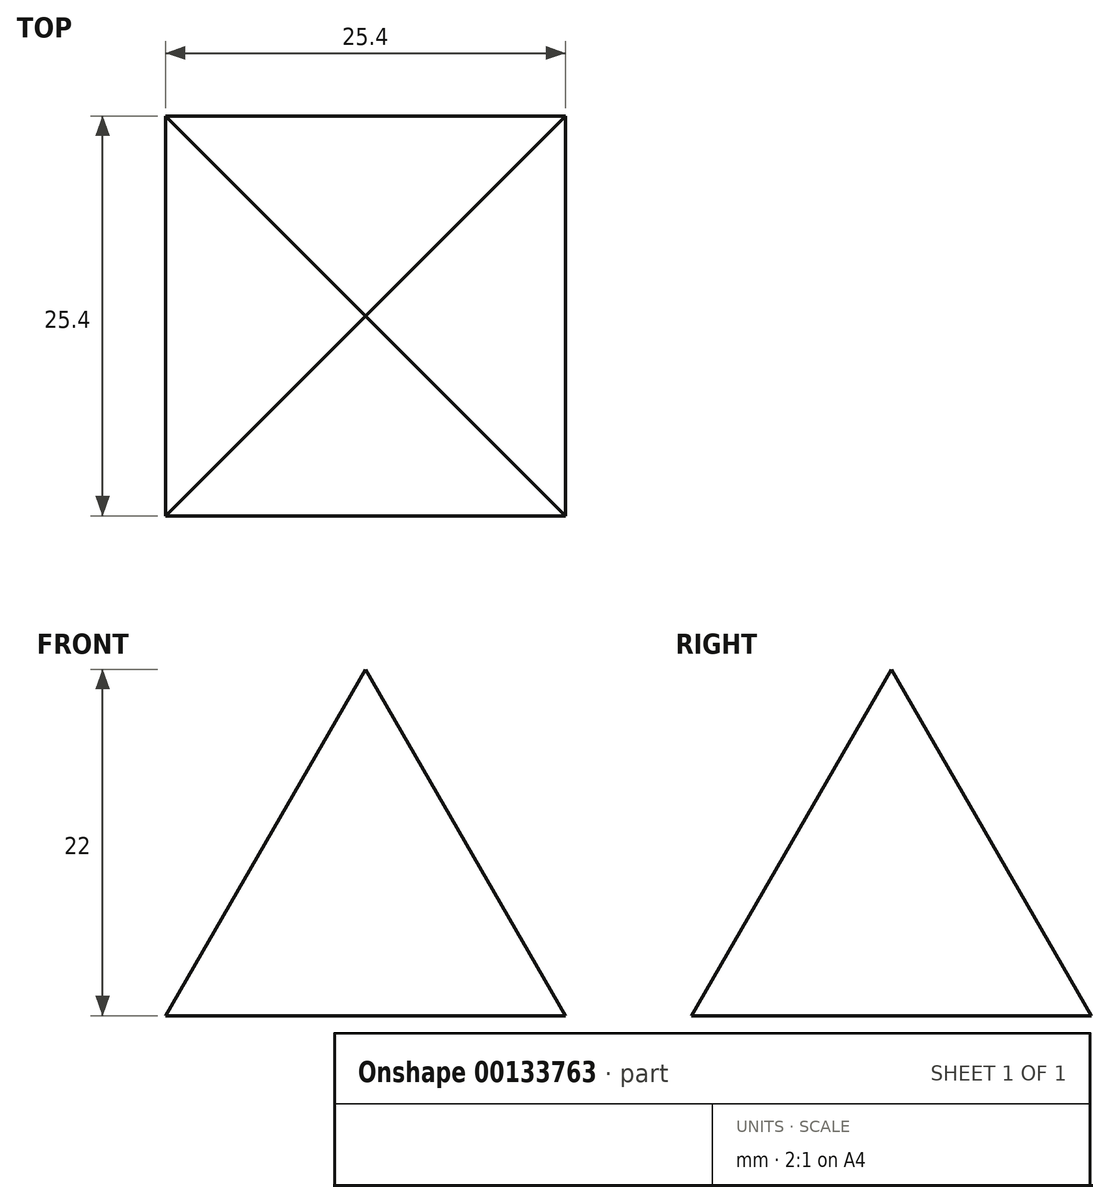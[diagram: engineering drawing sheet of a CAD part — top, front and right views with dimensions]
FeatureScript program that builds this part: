
annotation { "Feature Type Name" : "Feature", "Feature Type Description" : "" }
export const myFeature = defineFeature(function(context is Context, id is Id, definition is map)
    precondition{}
    {
        {
            var Q0;
            Q0=qCreatedBy(makeId("Top.planeOp"),FACE);
            var sketch = newSketch(context, id + "F0", { "sketchPlane" : qUnion([Q0])});
            skLineSegment(sketch, "E0.bottom", {"start": v(12.7, -12.7) * mm, "end": v(-12.7, -12.7) * mm});
            skLineSegment(sketch, "E0.top", {"start": v(12.7, 12.7) * mm, "end": v(-12.7, 12.7) * mm});
            skLineSegment(sketch, "E0.left", {"start": v(12.7, -12.7) * mm, "end": v(12.7, 12.7) * mm});
            skLineSegment(sketch, "E0.right", {"start": v(-12.7, -12.7) * mm, "end": v(-12.7, 12.7) * mm});
            skPoint(sketch, "E0.middle", {"position": v(0, 0) * mm});
            skSolve(sketch);
        }
        {
            var Q0;
            Q0=makeQuery(id+"F0.imprint","IMPRINT",FACE,{"disambiguationData":[TD([[makeQuery(id+"F0.imprint","IMPRINT",EDGE,{"derivedFrom":sQuery(id+"F0.wireOp",EDGE,"E0.bottom")}),-1.0]])]});
            extrude(context, id + "F1", {"entities" : qUnion([Q0]), "depth" : 25.4 * mm, "hasDraft" : true, "draftAngle" : 30 * degree, "draftPullDirection" : true});
        }
    });
